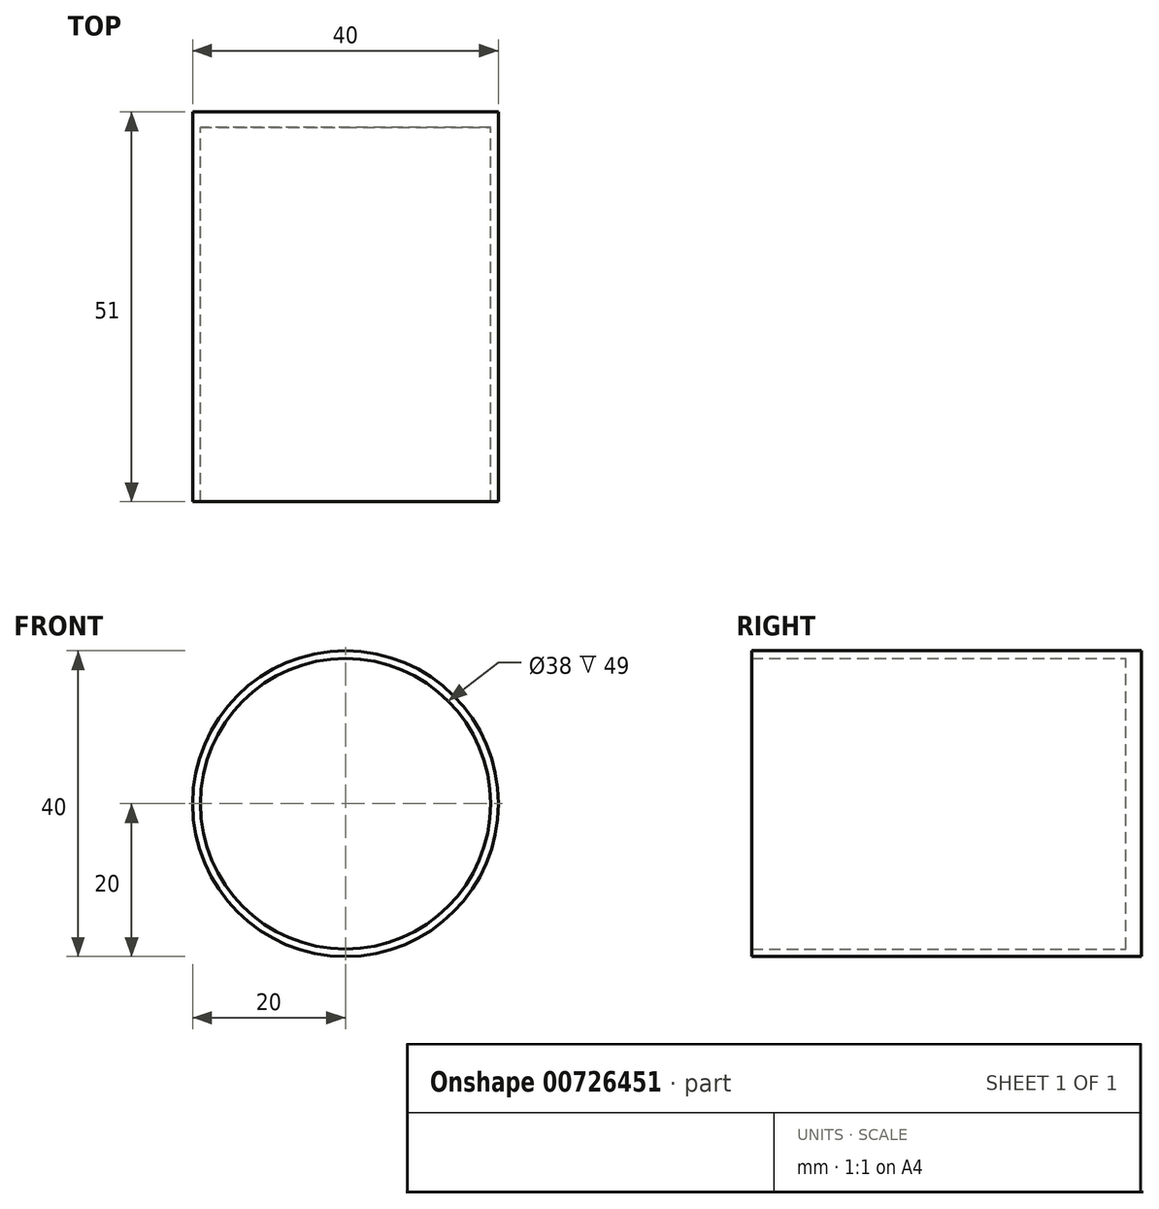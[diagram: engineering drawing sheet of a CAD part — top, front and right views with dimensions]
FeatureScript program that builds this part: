
annotation { "Feature Type Name" : "Feature", "Feature Type Description" : "" }
export const myFeature = defineFeature(function(context is Context, id is Id, definition is map)
    precondition{}
    {
        {
            var Q0;
            Q0=qCreatedBy(makeId("Front.planeOp"),FACE);
            var sketch = newSketch(context, id + "F0", { "sketchPlane" : qUnion([Q0])});
            skCircle(sketch, "E0", {"center": v(0, 0) * mm, "radius": 19 * mm});
            skCircle(sketch, "E1", {"center": v(0, 0) * mm, "radius": 20 * mm});
            skSolve(sketch);
        }
        {
            var Q0;
            Q0=makeQuery(id+"F0.imprint","IMPRINT",FACE,{"disambiguationData":[TD([[makeQuery(id+"F0.imprint","IMPRINT",EDGE,{"derivedFrom":sQuery(id+"F0.wireOp",EDGE,"E0")}),-1.0]])]});
            extrude(context, id + "F1", {"entities" : qUnion([Q0]), "depth" : 22 * mm, "offsetDistance" : 25 * mm});
        }
        {
            var Q0;
            Q0=makeQuery(id+"F1.opExtrude","CAP_FACE",FACE,{"disambiguationData":[OSD([sQuery(id+"F0.wireOp",EDGE,"E0"),sQuery(id+"F0.wireOp",EDGE,"E1")])],"isStart":false});
            var sketch = newSketch(context, id + "F2", { "sketchPlane" : qUnion([Q0])});
            skCircle(sketch, "E2", {"center": v(0, 0) * mm, "radius": 20 * mm});
            skCircle(sketch, "E3", {"center": v(0, 0) * mm, "radius": 19 * mm});
            skSolve(sketch);
        }
        {
            var Q0;
            Q0=makeQuery(id+"F2.imprint","IMPRINT",FACE,{"disambiguationData":[TD([[makeQuery(id+"F2.imprint","IMPRINT",EDGE,{"derivedFrom":sQuery(id+"F2.wireOp",EDGE,"E2")}),1.0]])]});
            extrude(context, id + "F3", {"entities" : qUnion([Q0]), "operationType" : NewBodyOperationType.ADD, "depth" : 27 * mm, "offsetDistance" : 25 * mm});
        }
        {
            var Q0;
            Q0=makeQuery(id+"F1.opExtrude","CAP_FACE",FACE,{"disambiguationData":[OSD([sQuery(id+"F0.wireOp",EDGE,"E0"),sQuery(id+"F0.wireOp",EDGE,"E1")])],"isStart":true});
            var sketch = newSketch(context, id + "F4", { "sketchPlane" : qUnion([Q0])});
            skCircle(sketch, "E4", {"center": v(0, 0) * mm, "radius": 20 * mm});
            skSolve(sketch);
        }
        {
            var Q0;
            Q0=makeQuery(id+"F4.imprint","IMPRINT",FACE,{"disambiguationData":[TD([[makeQuery(id+"F4.imprint","IMPRINT",EDGE,{"derivedFrom":makeQuery(id+"F1.opExtrude","CAP_EDGE",EDGE,{"disambiguationData":[OSD([sQuery(id+"F0.wireOp",EDGE,"E0")])],"isStart":true})}),-1.0]])]});
            var Q1;
            Q1=makeQuery(id+"F4.imprint","IMPRINT",FACE,{"disambiguationData":[TD([[makeQuery(id+"F4.imprint","IMPRINT",EDGE,{"derivedFrom":sQuery(id+"F4.wireOp",EDGE,"E4")}),-1.0]])]});
            extrude(context, id + "F5", {"entities" : qUnion([Q0, Q1]), "operationType" : NewBodyOperationType.ADD, "depth" : 2 * mm, "offsetDistance" : 25 * mm});
        }
    });
